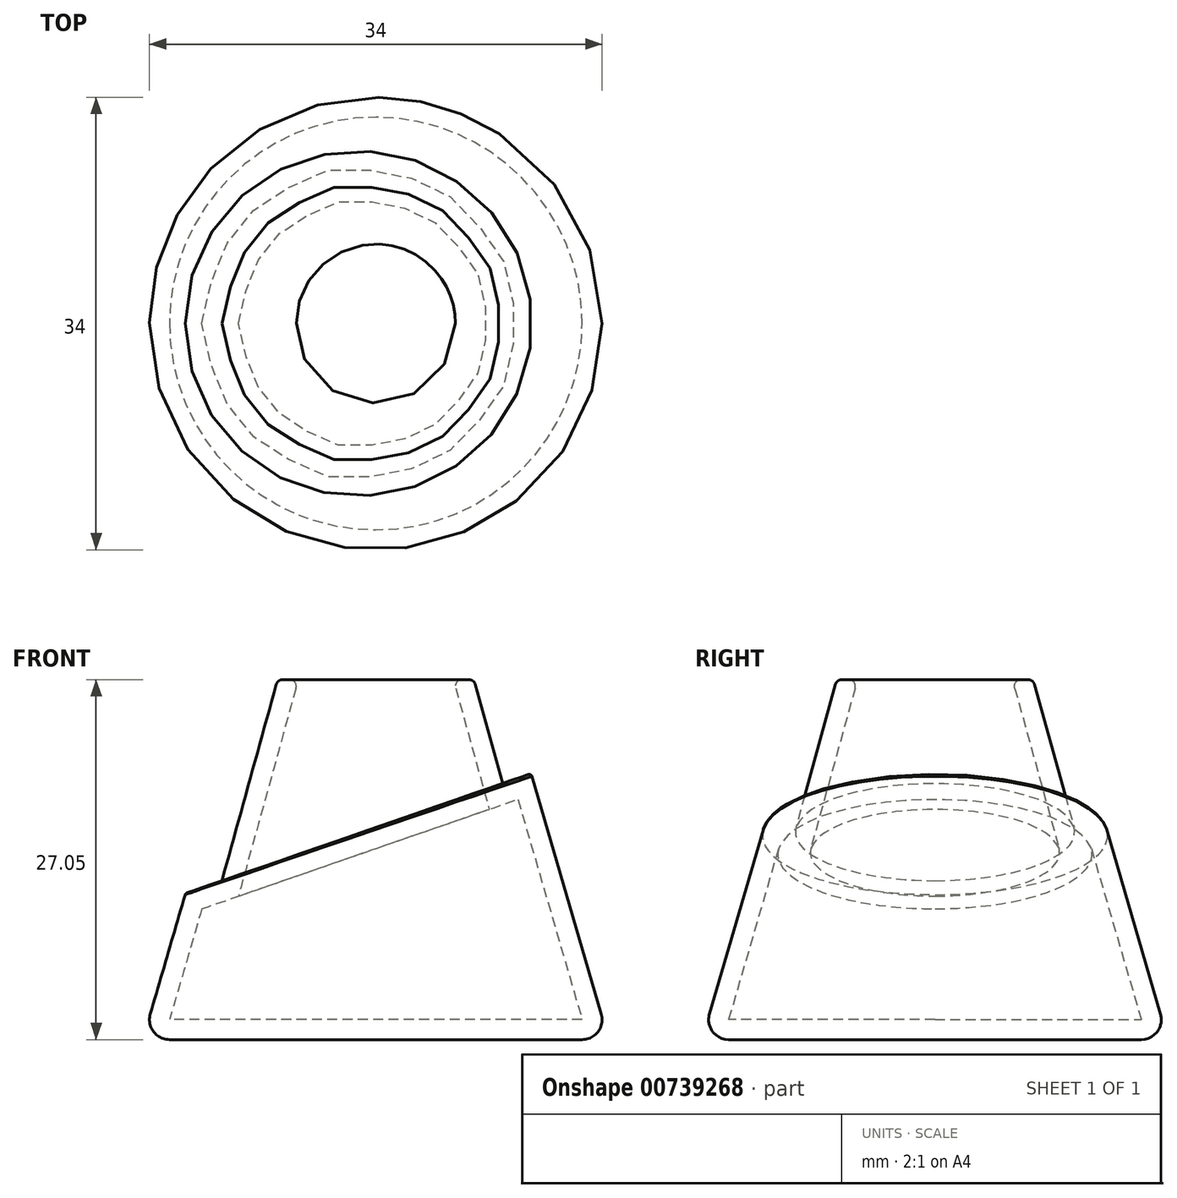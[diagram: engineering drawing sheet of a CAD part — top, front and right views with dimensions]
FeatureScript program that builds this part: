
annotation { "Feature Type Name" : "Feature", "Feature Type Description" : "" }
export const myFeature = defineFeature(function(context is Context, id is Id, definition is map)
    precondition{}
    {
        {
            var Q0;
            Q0=qCreatedBy(makeId("Front.planeOp"),FACE);
            var sketch = newSketch(context, id + "F0", { "sketchPlane" : qUnion([Q0])});
            skLineSegment(sketch, "E0", {"start": v(0, -27.05) * mm, "end": v(17.5, -27.05) * mm});
            skLineSegment(sketch, "E1", {"start": v(17.5, -27.05) * mm, "end": v(0, 32.95) * mm});
            skLineSegment(sketch, "E2", {"start": v(0, 32.95) * mm, "end": v(0, -27.05) * mm});
            skLineSegment(sketch, "E3", {"start": v(0, 38.42) * mm, "end": v(-0.1, -43.64) * mm});
            skSolve(sketch);
        }
        {
            var Q0;
            Q0=makeQuery(id+"F0.imprint","IMPRINT",FACE,{"disambiguationData":[TD([[makeQuery(id+"F0.imprint","IMPRINT",EDGE,{"derivedFrom":sQuery(id+"F0.wireOp",EDGE,"E0")}),1.0]])]});
            var Q1;
            Q1=sQuery(id+"F0.wireOp",EDGE,"E2");
            revolve(context, id + "F1", {"surfaceOperationType" : NewSurfaceOperationType.NEW, "entities" : qUnion([Q0]), "axis" : qUnion([Q1]), "revolveType" : RevolveType.FULL});
        }
        {
            var Q0;
            Q0=makeQuery(id+"F1.opRevolve","SWEPT_EDGE",EDGE,{"disambiguationData":[OSD([sQuery(id+"F0.wireOp",EDGE,"E0"),sQuery(id+"F0.wireOp",EDGE,"E1")])]});
            fillet(context, id + "F2", {"entities" : qUnion([Q0]), "radius" : 1.5 * mm, "tangentPropagation" : true, "allowEdgeOverflow" : false});
        }
        {
            var Q0;
            Q0=qCreatedBy(makeId("Front.planeOp"),FACE);
            cPlane(context, id + "F3", {"entities" : qUnion([Q0]), "cplaneType" : CPlaneType.OFFSET, "offset" : 25 * mm, "width" : 150 * mm, "height" : 150 * mm});
        }
        {
            var Q0;
            Q0=qCreatedBy(id+"F3.planeOp",FACE);
            var sketch = newSketch(context, id + "F4", { "sketchPlane" : qUnion([Q0])});
            skLineSegment(sketch, "E4", {"start": v(-14.46, -16.12) * mm, "end": v(11.74, -7.04) * mm});
            skLineSegment(sketch, "E5", {"start": v(11.74, -7.04) * mm, "end": v(20.6, -7.15) * mm});
            skLineSegment(sketch, "E6", {"start": v(20.6, -7.15) * mm, "end": v(20.73, 38.03) * mm});
            skLineSegment(sketch, "E7", {"start": v(20.73, 38.03) * mm, "end": v(-22.23, 38.53) * mm});
            skLineSegment(sketch, "E8", {"start": v(-22.23, 38.53) * mm, "end": v(-22.23, -16.07) * mm});
            skLineSegment(sketch, "E9", {"start": v(-22.23, -16.07) * mm, "end": v(-14.46, -16.12) * mm});
            skSolve(sketch);
        }
        {
            var Q0;
            Q0=makeQuery(id+"F4.imprint","IMPRINT",FACE,{"disambiguationData":[TD([[makeQuery(id+"F4.imprint","IMPRINT",EDGE,{"derivedFrom":sQuery(id+"F4.wireOp",EDGE,"E4")}),1.0]])]});
            extrude(context, id + "F5", {"entities" : qUnion([Q0]), "operationType" : NewBodyOperationType.REMOVE, "oppositeDirection" : true, "depth" : 56 * mm, "offsetDistance" : 25 * mm});
        }
        {
            var Q0;
            Q0=makeQuery(id+"F5.boolean.opBoolean","COPY",FACE,{"derivedFrom":makeQuery(id+"F5.opExtrude","SWEPT_FACE",FACE,{"disambiguationData":[OSD([sQuery(id+"F4.wireOp",EDGE,"E4")])]})});
            shell(context, id + "F6", {"entities" : qUnion([Q0]), "thickness" : 2.5 * mm});
        }
        {
            var Q0;
            Q0=makeQuery(id+"F5.boolean.opBoolean","INTERSECT",EDGE,{"derivedFrom":[makeQuery(id+"F1.opRevolve","SWEPT_FACE",FACE,{"disambiguationData":[OSD([sQuery(id+"F0.wireOp",EDGE,"E1")])]}),makeQuery(id+"F5.opExtrude","SWEPT_FACE",FACE,{"disambiguationData":[OSD([sQuery(id+"F4.wireOp",EDGE,"E4")])]})]});
            fillet(context, id + "F7", {"entities" : qUnion([Q0]), "radius" : .2 * mm, "tangentPropagation" : true, "allowEdgeOverflow" : false});
        }
        {
            var Q0;
            Q0=qCreatedBy(makeId("Top.planeOp"),FACE);
            var sketch = newSketch(context, id + "F8", { "sketchPlane" : qUnion([Q0])});
            skCircle(sketch, "E10", {"center": v(0, 0) * mm, "radius": 7.38 * mm});
            skSolve(sketch);
        }
        {
            var Q1;
            Q1=makeQuery(id+"F6.opShell","OFFSET_FACE",FACE,{"disambiguationData":[OSD([sQuery(id+"F0.wireOp",EDGE,"E0")])]});
            var Q2;
            Q2=makeQuery(id+"F8.imprint","IMPRINT",FACE,{"disambiguationData":[TD([[makeQuery(id+"F8.imprint","IMPRINT",EDGE,{"derivedFrom":sQuery(id+"F8.wireOp",EDGE,"E10")}),1.0]])]});
            loft(context, id + "F9", {"operationType" : NewBodyOperationType.ADD, "sheetProfilesArray" : [{ "sheetProfileEntities" : qUnion([Q1]) }, { "sheetProfileEntities" : qUnion([Q2]) }]});
        }
        {
            var Q0;
            Q0=makeQuery(id+"F9.opLoft","CAP_FACE",FACE,{"disambiguationData":[OSD([makeQuery(id+"F8.imprint","IMPRINT",FACE,{"disambiguationData":[TD([[makeQuery(id+"F8.imprint","IMPRINT",EDGE,{"derivedFrom":sQuery(id+"F8.wireOp",EDGE,"E10")}),1.0]])]})])],"isStart":true});
            shell(context, id + "F10", {"entities" : qUnion([Q0]), "thickness" : 1.5 * mm});
        }
        {
            var Q0;
            Q0=makeQuery(id+"F9.opLoft","MID_CAP_EDGE",EDGE,{"disambiguationData":[OSD([sQuery(id+"F8.wireOp",EDGE,"E10")])],"capPos":1.0});
            fillet(context, id + "F11", {"entities" : qUnion([Q0]), "radius" : .5 * mm, "tangentPropagation" : true, "allowEdgeOverflow" : false});
        }
        {
            var Q0;
            Q0=makeQuery(id+"F10.opShell","OFFSET_EDGE",EDGE,{"disambiguationData":[OSD([sQuery(id+"F8.wireOp",EDGE,"E10")])]});
            fillet(context, id + "F12", {"entities" : qUnion([Q0]), "radius" : .5 * mm, "tangentPropagation" : true, "allowEdgeOverflow" : false});
        }
    });
